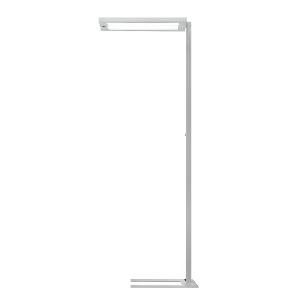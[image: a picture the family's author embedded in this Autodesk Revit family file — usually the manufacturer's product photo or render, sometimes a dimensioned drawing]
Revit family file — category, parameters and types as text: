
# Revit family: lavigo_core_-_dps_12500_840_r_g1_ws_00812431_16fd
name_source: partatom
category: Lighting Fixtures
units: mm (PartAtom-declared; Revit-internal decimal feet)

## family parameters
Cut with Voids When Loaded = No
Host = Face
Light Source = No
Part Type = Normal
Room Calculation Point = No
Round Connector Dimension = Use Diameter
Shared = No

## types (1)
- LAVIGO.core - DPS 12500/840/R/G1/WS (1 x LED, 12400 lm, 4000K)
    Apparent Load = 85 VA
    Approval mark = CE
    CIE Flux Codes = 58 87 97 17 100
    Color Rendering = 80-89
    Color Temperature = 4000K
    Control Gear = Electronic ballast
    Default Elevation = 1800 mm
    Description = DPS 12500/840/R/G1|Free-standing luminaire|light source: LED Cold white   |work equipment: Electronic ballast DALI|connected load: 220-240 V, 50/60 Hz|Power consumption: approx. 85 W|standby: approx. 0,30|power factor: approx. 0,973|luminous flux: 12400 lm|luminous efficacy: 145 lm/W|light distribution: Direct/indirect|direct ratio: approx. 17 %|color rendering index (CRI): >= 80|chromaticity tolerance:  3 SDCM|technology: Presence and daylight sensor control (PIR)|operation: Rocker switch|luminaire body|material: Steel/plastic|surface: Painted|colour: White|lamp cover: Polycarbonate (PC), Clear|tubular section|material: Steel tube|surface: Painted|Form: Tubular section upright|colour of tubular section: White|luminaire base|Form: C-form flat|weight (net): approx. 14.7 kg|mains lead: 3.00 m Mains plug CEE 7/VII|Fastening: Floor standing base|decorative contrast side parts: Flint grey|glare control: Prism aperture|luminance(L65): <= 3000 cd/m|unified glare rating(4H 8H): <=  16|special features: Luminaire head detachable, Direct and indirect light switchable together, Flicker-free, Integrated light and presence sensor PIR, Motion sensor time-out of 15mins~|Approval mark: US~B_0014~VDE - ENEC|
    Frequency = 50 Hz, 60 Hz
    Height = 36 mm
    Lamp = 1 x LED
    Lamp Light Flux = 12400 lm
    Lamp count = 1
    Length = 675 mm
    Luminous efficacy = 146 lm/W
    Manufacturer = Waldmann
    ModVariant = No
    Model = 00812431
    Mounting Place = Floor
    Mounting Type = Freestanding
    Number of Poles = 1
    OnlyDefault = Yes
    Power Factor = 1
    Product Name = LAVIGO.core - DPS 12500/840/R/G1/WS
    Product group = Free standing luminaire
    ProductGroupID = 13
    Protection Class = Protection class I
    Protection Degree = IP 20
    RLX_Detail_Level = 1
    RLX_Emergency_Light_Flux = 0 lm
    RLX_Emergency_Type = 0
    RLX_Emergency_Type_DB = No
    RlxData = <blob elided: 32189 chars, md5=07f4a7d7>
    Socket = socket
    Standby Power = 0 W
    System Light Flux = 12400 lm
    System Power = 85 W
    Type Comments = Product without accessories
    Type Image = 121805000-00747395.jpg
    URL = http://relux.com
    VarID = ---
    Voltage = 230 V
    Voltage Range = 220-240 V
    Weight = 0.00 kg
    Width = 320 mm

## geometry (parser evidence)
native form markers: Blend x4, Sweep x14
no freeform markers — native parametric forms only
